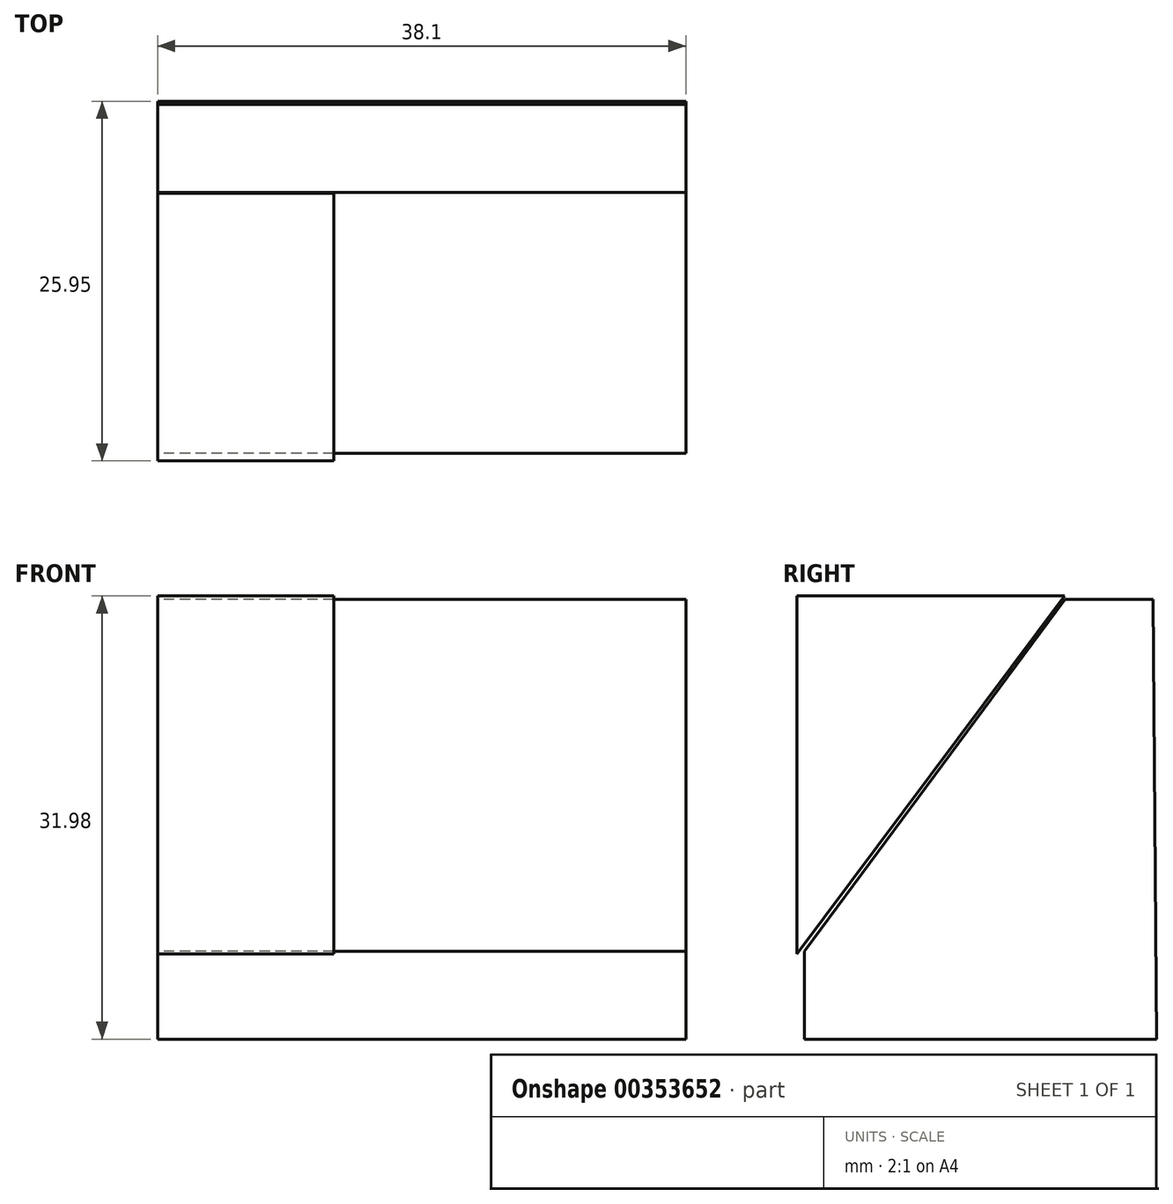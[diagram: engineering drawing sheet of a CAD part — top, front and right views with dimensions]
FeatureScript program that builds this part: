
annotation { "Feature Type Name" : "Feature", "Feature Type Description" : "" }
export const myFeature = defineFeature(function(context is Context, id is Id, definition is map)
    precondition{}
    {
        {
            var Q0;
            Q0=qCreatedBy(makeId("Right.planeOp"),FACE);
            var sketch = newSketch(context, id + "F0", { "sketchPlane" : qUnion([Q0])});
            skLineSegment(sketch, "E0", {"start": v(-56.36, 0) * mm, "end": v(-56.36, 6.35) * mm});
            skLineSegment(sketch, "E1", {"start": v(-56.36, 6.35) * mm, "end": v(-37.55, 31.75) * mm});
            skLineSegment(sketch, "E2", {"start": v(-37.55, 31.75) * mm, "end": v(-31.2, 31.75) * mm});
            skLineSegment(sketch, "E3", {"start": v(-31.2, 31.75) * mm, "end": v(-30.96, 0) * mm});
            skLineSegment(sketch, "E4", {"start": v(-56.36, 0) * mm, "end": v(-30.96, 0) * mm});
            skSolve(sketch);
        }
        {
            var Q0;
            Q0=makeQuery(id+"F0.imprint","IMPRINT",FACE,{"disambiguationData":[TD([[makeQuery(id+"F0.imprint","IMPRINT",EDGE,{"derivedFrom":sQuery(id+"F0.wireOp",EDGE,"E0")}),-1.0]])]});
            extrude(context, id + "F1", {"entities" : qUnion([Q0]), "depth" : 38.1 * mm});
        }
        {
            var Q0;
            Q0=qCreatedBy(makeId("Right.planeOp"),FACE);
            var sketch = newSketch(context, id + "F2", { "sketchPlane" : qUnion([Q0])});
            skLineSegment(sketch, "E5", {"start": v(-37.6, 31.98) * mm, "end": v(-56.9, 31.98) * mm});
            skLineSegment(sketch, "E6", {"start": v(-56.9, 31.98) * mm, "end": v(-56.9, 0) * mm});
            skLineSegment(sketch, "E7", {"start": v(-37.6, 31.98) * mm, "end": v(-56.9, 6.13) * mm});
            skSolve(sketch);
        }
        {
            var Q0;
            {var subQ0=sQuery(id+"F2.wireOp",EDGE,"E5");Q0=makeQuery(id+"F2.imprint","IMPRINT",FACE,{"disambiguationData":[TD([[makeQuery(id+"F2.imprint","IMPRINT",EDGE,{"derivedFrom":subQ0}),1.0]])]});}
            extrude(context, id + "F3", {"entities" : qUnion([Q0]), "depth" : 12.7 * mm});
        }
    });
